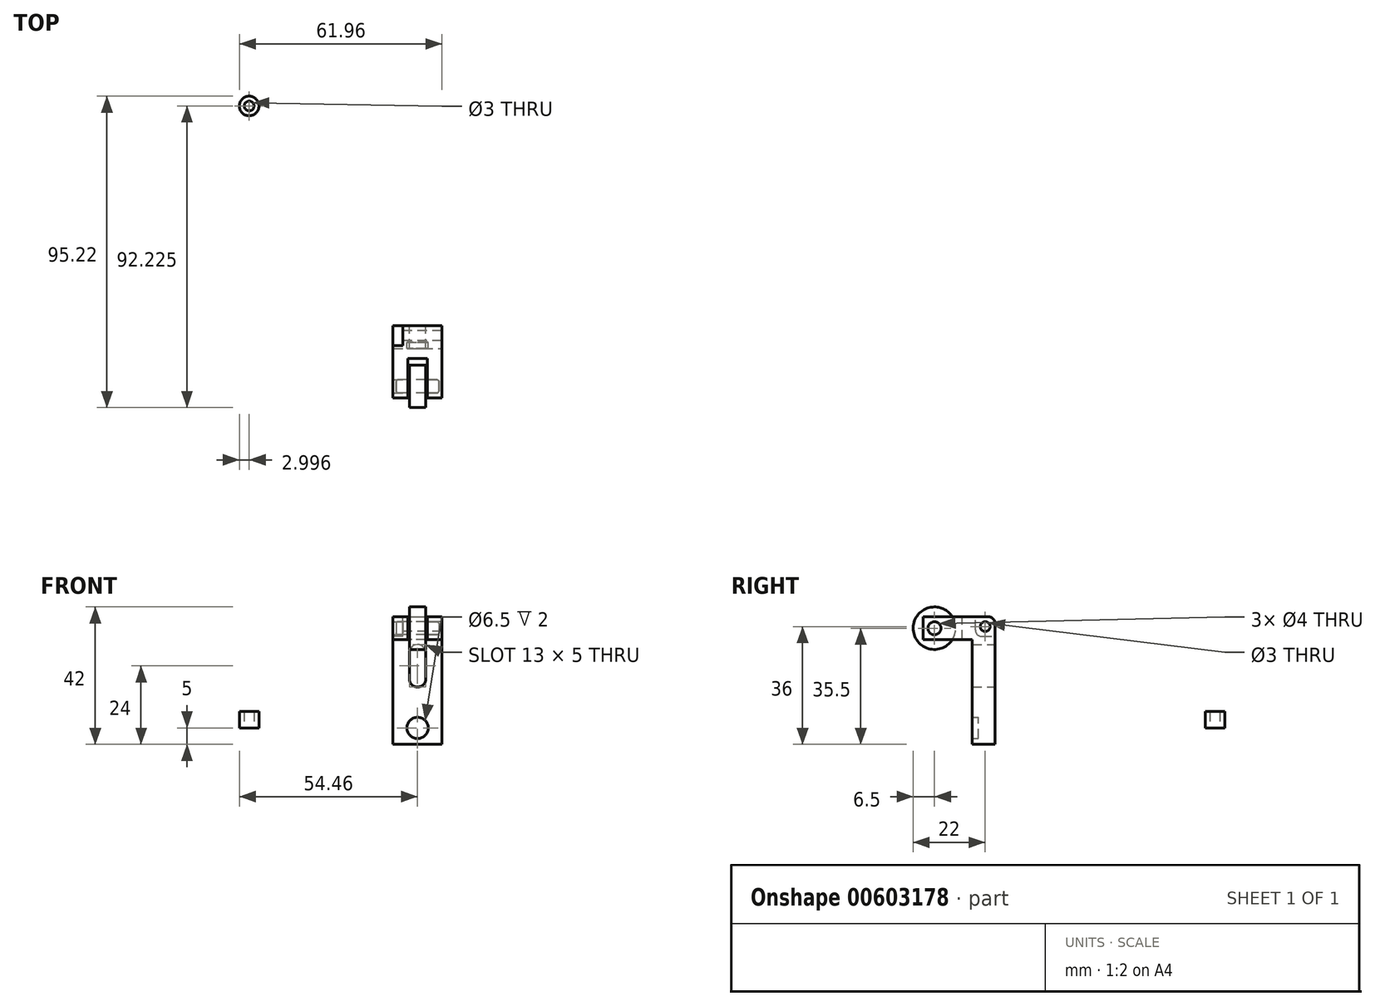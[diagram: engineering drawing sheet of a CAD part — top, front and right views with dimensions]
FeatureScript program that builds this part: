
annotation { "Feature Type Name" : "Feature", "Feature Type Description" : "" }
export const myFeature = defineFeature(function(context is Context, id is Id, definition is map)
    precondition{}
    {
        {
            var Q0;
            Q0=qCreatedBy(makeId("Front.planeOp"),FACE);
            var sketch = newSketch(context, id + "F0", { "sketchPlane" : qUnion([Q0])});
            skLineSegment(sketch, "E0", {"start": v(-7.5, 27) * mm, "end": v(-7.5, -5) * mm});
            skLineSegment(sketch, "E1", {"start": v(-7.5, -5) * mm, "end": v(7.5, -5) * mm});
            skLineSegment(sketch, "E2", {"start": v(7.5, -5) * mm, "end": v(7.5, 27) * mm});
            skLineSegment(sketch, "E3", {"start": v(7.5, 27) * mm, "end": v(-7.5, 27) * mm});
            skLineSegment(sketch, "E4", {"start": v(-7.5, 27) * mm, "end": v(-7.5, 34) * mm});
            skLineSegment(sketch, "E5", {"start": v(-7.5, 34) * mm, "end": v(7.5, 34) * mm});
            skLineSegment(sketch, "E6", {"start": v(7.5, 34) * mm, "end": v(7.5, 27) * mm});
            skPoint(sketch, "E7", {"position": v(0, 0) * mm});
            skLineSegment(sketch, "E8", {"start": v(2.5, 23) * mm, "end": v(2.5, 15) * mm});
            skLineSegment(sketch, "E9", {"start": v(-2.5, 23) * mm, "end": v(-2.5, 15) * mm});
            skArc(sketch, "E10", {"start": v(2.5, 23) * mm, "mid": v(0, 25.5) * mm, "end": v(-2.5, 23) * mm});
            skArc(sketch, "E11", {"start": v(2.5, 15) * mm, "mid": v(0, 12.5) * mm, "end": v(-2.5, 15) * mm});
            skCircle(sketch, "E12", {"center": v(0, 0) * mm, "radius": 3.25 * mm});
            skLineSegment(sketch, "E13", {"start": v(3, 27) * mm, "end": v(3, 34) * mm});
            skLineSegment(sketch, "E14", {"start": v(-3, 27) * mm, "end": v(-3, 34) * mm});
            skSolve(sketch);
        }
        {
            var Q0;
            Q0=makeQuery(id+"F0.imprint","IMPRINT",FACE,{"disambiguationData":[TD([[makeQuery(id+"F0.imprint","IMPRINT",EDGE,{"derivedFrom":sQuery(id+"F0.wireOp",EDGE,"E0")}),1.0]])]});
            extrude(context, id + "F1", {"entities" : qUnion([Q0]), "depth" : 7 * mm, "offsetDistance" : 25 * mm});
        }
        {
            var Q0;
            {var subQ0=sQuery(id+"F0.wireOp",EDGE,"E4");Q0=makeQuery(id+"F0.imprint","IMPRINT",FACE,{"disambiguationData":[TD([[makeQuery(id+"F0.imprint","IMPRINT",EDGE,{"derivedFrom":subQ0}),-1.0]])]});}
            var Q1;
            {var subQ0=sQuery(id+"F0.wireOp",EDGE,"E6");Q1=makeQuery(id+"F0.imprint","IMPRINT",FACE,{"disambiguationData":[TD([[makeQuery(id+"F0.imprint","IMPRINT",EDGE,{"derivedFrom":subQ0}),-1.0]])]});}
            extrude(context, id + "F2", {"entities" : qUnion([Q0, Q1]), "operationType" : NewBodyOperationType.ADD, "depth" : 22 * mm, "offsetDistance" : 25 * mm});
        }
        {
            var Q0;
            Q0=makeQuery(id+"F0.imprint","IMPRINT",FACE,{"disambiguationData":[TD([[makeQuery(id+"F0.imprint","IMPRINT",EDGE,{"derivedFrom":sQuery(id+"F0.wireOp",EDGE,"E12")}),1.0]])]});
            extrude(context, id + "F3", {"entities" : qUnion([Q0]), "operationType" : NewBodyOperationType.ADD, "depth" : 5 * mm, "offsetDistance" : 25 * mm});
        }
        {
            var Q0;
            {var subQ0=sQuery(id+"F0.wireOp",EDGE,"E13");Q0=makeQuery(id+"F0.imprint","IMPRINT",FACE,{"disambiguationData":[TD([[makeQuery(id+"F0.imprint","IMPRINT",EDGE,{"derivedFrom":subQ0}),1.0]])]});}
            extrude(context, id + "F4", {"entities" : qUnion([Q0]), "operationType" : NewBodyOperationType.ADD, "depth" : 10 * mm, "offsetDistance" : 25 * mm});
        }
        {
            var Q0;
            {var subQ0=sQuery(id+"F0.wireOp",EDGE,"E5");Q0=makeQuery(id+"F4.boolean.opBoolean","MERGE",EDGE,{"derivedFrom":[makeQuery(id+"F2.opExtrude","CAP_EDGE",EDGE,{"disambiguationData":[OSD([subQ0]),TDD([makeQuery(id+"F0.imprint","IMPRINT",EDGE,{"disambiguationData":[TD([[makeQuery(id+"F0.imprint","INTERSECT",VERTEX,{"derivedFrom":[sQuery(id+"F0.wireOp",EDGE,"E4"),subQ0]}),-1.0]])],"derivedFrom":subQ0})])],"isStart":true}),makeQuery(id+"F2.opExtrude","CAP_EDGE",EDGE,{"disambiguationData":[OSD([subQ0]),TDD([makeQuery(id+"F0.imprint","IMPRINT",EDGE,{"disambiguationData":[TD([[makeQuery(id+"F0.imprint","INTERSECT",VERTEX,{"derivedFrom":[subQ0,sQuery(id+"F0.wireOp",EDGE,"E6")]}),1.0]])],"derivedFrom":subQ0})])],"isStart":true}),makeQuery(id+"F4.opExtrude","CAP_EDGE",EDGE,{"disambiguationData":[OSD([subQ0])],"isStart":true})]});}
            var Q1;
            {var subQ0=sQuery(id+"F0.wireOp",EDGE,"E3");var subQ4=makeQuery(id+"F1.opExtrude","CAP_EDGE",EDGE,{"disambiguationData":[OSD([subQ0])],"isStart":false});Q1=makeQuery(id+"F4.boolean.opBoolean","MERGE",EDGE,{"derivedFrom":[makeQuery(id+"F2.boolean.opBoolean","SPLIT",EDGE,{"disambiguationData":[topologyDisambiguationEdgeConnected([makeQuery(id+"F2.opExtrude","SWEPT_FACE",FACE,{"disambiguationData":[OSD([subQ0]),TDD([makeQuery(id+"F0.imprint","IMPRINT",EDGE,{"disambiguationData":[TD([[makeQuery(id+"F0.imprint","INTERSECT",VERTEX,{"derivedFrom":[subQ0,sQuery(id+"F0.wireOp",EDGE,"E14")]}),-1.0]])],"derivedFrom":subQ0})])]})])],"derivedFrom":subQ4}),makeQuery(id+"F2.boolean.opBoolean","SPLIT",EDGE,{"disambiguationData":[topologyDisambiguationEdgeConnected([makeQuery(id+"F2.opExtrude","SWEPT_FACE",FACE,{"disambiguationData":[OSD([subQ0]),TDD([makeQuery(id+"F0.imprint","IMPRINT",EDGE,{"disambiguationData":[TD([[makeQuery(id+"F0.imprint","INTERSECT",VERTEX,{"derivedFrom":[subQ0,sQuery(id+"F0.wireOp",EDGE,"E13")]}),1.0]])],"derivedFrom":subQ0})])]})])],"derivedFrom":subQ4}),makeQuery(id+"F2.boolean.opBoolean","SPLIT",EDGE,{"disambiguationData":[topologyDisambiguationEdgeConnected([makeQuery(id+"F1.opExtrude","SWEPT_FACE",FACE,{"disambiguationData":[OSD([subQ0])]})])],"derivedFrom":subQ4})]});}
            fillet(context, id + "F5", {"entities" : qUnion([Q0, Q1]), "radius" : 2 * mm, "tangentPropagation" : true, "allowEdgeOverflow" : false});
        }
        {
            var Q0;
            Q0=makeQuery(id+"F2.boolean.opBoolean","MERGE",FACE,{"derivedFrom":[makeQuery(id+"F1.opExtrude","SWEPT_FACE",FACE,{"disambiguationData":[OSD([sQuery(id+"F0.wireOp",EDGE,"E0")])]}),makeQuery(id+"F2.opExtrude","SWEPT_FACE",FACE,{"disambiguationData":[OSD([sQuery(id+"F0.wireOp",EDGE,"E4")])]})]});
            var sketch = newSketch(context, id + "F6", { "sketchPlane" : qUnion([Q0])});
            skLineSegment(sketch, "E15.0", {"start": v(22, 27) * mm, "end": v(22, 34) * mm});
            skPoint(sketch, "E16", {"position": v(18.5, 30.5) * mm});
            skLineSegment(sketch, "E17", {"start": v(4, 28) * mm, "end": v(0, 28) * mm});
            skLineSegment(sketch, "E18", {"start": v(6, 30) * mm, "end": v(6, 34) * mm});
            skLineSegment(sketch, "E19", {"start": v(6, 34) * mm, "end": v(0, 34) * mm});
            skLineSegment(sketch, "E20", {"start": v(0, 34) * mm, "end": v(0, 28) * mm});
            skPoint(sketch, "E21.visualSharp", {"position": v(6, 28) * mm});
            skArc(sketch, "E21.filletArc", {"start": v(4, 28) * mm, "mid": v(5.41, 28.59) * mm, "end": v(6, 30) * mm});
            skCircle(sketch, "E22", {"center": v(3, 31) * mm, "radius": 1.5 * mm});
            skCircle(sketch, "E23", {"center": v(18.5, 30.5) * mm, "radius": 6.5 * mm});
            skCircle(sketch, "E24", {"center": v(18.5, 30.5) * mm, "radius": 2 * mm});
            skLineSegment(sketch, "E25", {"start": v(-27.02, 67.3) * mm, "end": v(54.6, 67.3) * mm, "construction": true});
            skSolve(sketch);
        }
        {
            var Q0;
            Q0=sQuery(id+"F6.wireOp",VERTEX,"E16");
            var Q1;
            Q1=makeQuery(id+"F1.opExtrude","SWEPT_BODY",BODY,{"disambiguationData":[OSD([sQuery(id+"F0.wireOp",EDGE,"E0"),sQuery(id+"F0.wireOp",EDGE,"E1"),sQuery(id+"F0.wireOp",EDGE,"E2"),sQuery(id+"F0.wireOp",EDGE,"E3"),sQuery(id+"F0.wireOp",EDGE,"E8"),sQuery(id+"F0.wireOp",EDGE,"E9"),sQuery(id+"F0.wireOp",EDGE,"E10"),sQuery(id+"F0.wireOp",EDGE,"E11"),sQuery(id+"F0.wireOp",EDGE,"E12")])]});
            hole(context, id + "F7", {"style" : HoleStyle.SIMPLE, "endStyle" : HoleEndStyle.BLIND, "holeDiameter" : 4 * mm, "majorDiameter" : 5 * mm, "holeDepth" : 20 * mm, "isTappedThrough" : true, "tappedDepth" : 12 * mm, "tapClearance" : 3, "locations" : qUnion([Q0]), "scope" : qUnion([Q1])});
        }
        {
            var Q0;
            Q0=makeQuery(id+"F6.imprint","IMPRINT",FACE,{"disambiguationData":[TD([[makeQuery(id+"F6.imprint","IMPRINT",EDGE,{"derivedFrom":sQuery(id+"F6.wireOp",EDGE,"E22")}),1.0]])]});
            extrude(context, id + "F8", {"entities" : qUnion([Q0]), "operationType" : NewBodyOperationType.REMOVE, "oppositeDirection" : true, "depth" : 25 * mm, "offsetDistance" : 25 * mm});
        }
        {
            var Q0;
            {var subQ7=sQuery(id+"F6.wireOp",EDGE,"E17");Q0=makeQuery(id+"F6.imprint","IMPRINT",FACE,{"disambiguationData":[TD([[makeQuery(id+"F6.imprint","IMPRINT",EDGE,{"derivedFrom":subQ7}),-1.0]])]});}
            extrude(context, id + "F9", {"entities" : qUnion([Q0]), "operationType" : NewBodyOperationType.REMOVE, "oppositeDirection" : true, "depth" : 3 * mm, "offsetDistance" : 25 * mm});
        }
        {
            var Q0;
            {var subQ0=sQuery(id+"F6.wireOp",EDGE,"E15.0");Q0=makeQuery(id+"F6.imprint","IMPRINT",FACE,{"disambiguationData":[TD([[makeQuery(id+"F6.imprint","IMPRINT",EDGE,{"derivedFrom":subQ0}),-1.0]])]});}
            var Q1;
            {var subQ0=sQuery(id+"F6.wireOp",EDGE,"E15.0");Q1=makeQuery(id+"F6.imprint","IMPRINT",FACE,{"disambiguationData":[TD([[makeQuery(id+"F6.imprint","IMPRINT",EDGE,{"derivedFrom":subQ0}),1.0]])]});}
            extrude(context, id + "F10", {"entities" : qUnion([Q0, Q1]), "oppositeDirection" : true, "depth" : 10 * mm, "offsetDistance" : 25 * mm, "hasSecondDirection" : true, "secondDirectionOppositeDirection" : true, "secondDirectionDepth" : 5 * mm});
        }
        {
            var Q0;
            Q0=makeQuery(id+"F6.imprint","IMPRINT",FACE,{"disambiguationData":[TD([[makeQuery(id+"F6.imprint","IMPRINT",EDGE,{"derivedFrom":sQuery(id+"F6.wireOp",EDGE,"E24")}),1.0]])]});
            extrude(context, id + "F11", {"entities" : qUnion([Q0]), "oppositeDirection" : true, "depth" : 14 * mm, "offsetDistance" : 25 * mm, "hasSecondDirection" : true, "secondDirectionOppositeDirection" : true, "secondDirectionDepth" : 1 * mm});
        }
        {
            var Q0;
            Q0=makeQuery(id+"F11.opExtrude","CAP_EDGE",EDGE,{"disambiguationData":[OSD([sQuery(id+"F6.wireOp",EDGE,"E24")])],"isStart":true});
            fillet(context, id + "F12", {"entities" : qUnion([Q0]), "radius" : .5 * mm, "tangentPropagation" : true, "allowEdgeOverflow" : false});
        }
        {
            var Q0;
            Q0=makeQuery(id+"F11.opExtrude","CAP_EDGE",EDGE,{"disambiguationData":[OSD([sQuery(id+"F6.wireOp",EDGE,"E24")])],"isStart":false});
            fillet(context, id + "F13", {"entities" : qUnion([Q0]), "radius" : .5 * mm, "tangentPropagation" : true, "allowEdgeOverflow" : false});
        }
        {
            var Q0;
            Q0=qCreatedBy(makeId("Top.planeOp"),FACE);
            var sketch = newSketch(context, id + "F14", { "sketchPlane" : qUnion([Q0])});
            skCircle(sketch, "E26", {"center": v(-51.46, 67.22) * mm, "radius": 1.5 * mm});
            skCircle(sketch, "E27", {"center": v(-51.46, 67.22) * mm, "radius": 3 * mm});
            skSolve(sketch);
        }
        {
            var Q0;
            Q0=makeQuery(id+"F14.imprint","IMPRINT",FACE,{"disambiguationData":[TD([[makeQuery(id+"F14.imprint","IMPRINT",EDGE,{"derivedFrom":sQuery(id+"F14.wireOp",EDGE,"E26")}),-1.0]])]});
            extrude(context, id + "F15", {"entities" : qUnion([Q0]), "depth" : 5 * mm, "offsetDistance" : 25 * mm});
        }
    });
